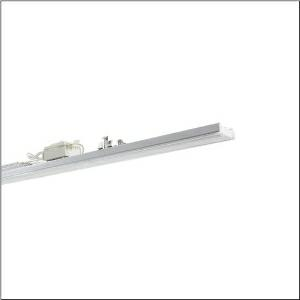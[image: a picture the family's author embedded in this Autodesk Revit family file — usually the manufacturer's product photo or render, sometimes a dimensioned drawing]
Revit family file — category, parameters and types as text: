
# Revit family: licross_r__21_recessed_ho_52tl1edn4e5s_7fa6
name_source: partatom
category: Lighting Fixtures
units: mm (PartAtom-declared; Revit-internal decimal feet)

## family parameters
Cut with Voids When Loaded = No
Host = Face
Light Source = No
Part Type = Normal
Room Calculation Point = No
Round Connector Dimension = Use Diameter
Shared = No

## types (1)
- --- (1 x LED, 14620 lm, 84.6 W, 4000K)
    Apparent Load = 85 VA
    CIE Flux Codes = 85 95 99 100 100
    Color Rendering = 80
    Color Temperature = 4000K
    Default Elevation = 1800 mm
    Description = Licross® 21 Recessed HO, luminaire insert, of sheet steel, galvanised, coil coated, white, length: 1.500mm, width: 66mm, height: 67mm, LED rated luminous flux: 14.620lm, light colour: 840, control gear: DALI 2, with plug, 5-pole, with phase selection, mains connection: 220..240V, AC, 50/60Hz, rated input power: 85W, internal wiring halogen-free, primary light control with lens, of plastic, primary optical cover: cover, of PMMA, light emission: direct distribution, primary light characteristic: symmetric, protection rating (complete): IP40, insulation class (complete): insulation class I (protective earthing), certification: CE, ENEC, VDE, UKCA, protection symbol: D if used in an environment without relevant dust loads with corresponding accessories, impact resistance: IK06, permissible ambient temperature for indoor applications: -25..+30°C, corresponds to IFS (International Featured Standards) requirements for safety and quality in the food industry, reducing of maximum allowable ambient temperature of 5°C with ceiling mounting, LABS conformity tested according to VDMA 24364:2018-05, packaging unit: 1 piece
    Height = 58 mm
    Lamp = 1 x LED
    Lamp Light Flux = 14620 lm
    Lamp Power = 84.6 W
    Lamp count = 1
    Length = 1500 mm
    Luminous efficacy = 173 lm/W
    Manufacturer = Siteco
    ModVariant = No
    Model = 52TL1EDN4E5S
    Mounting Place = Ceiling
    Mounting Type = Pendant
    Number of Poles = 1
    OnlyDefault = Yes
    Power Factor = 1
    Product Name = Licross® 21 Recessed HO
    Product group = luminaire insert | ceiling pendant
    ProductGroupID = 902
    Protection Class = Protection class I
    Protection Degree = IP 40
    RLX_Detail_Level = 1
    RLX_Emergency_Light_Flux = 0 lm
    RLX_Emergency_Type = 0
    RLX_Emergency_Type_DB = No
    RlxData = <blob elided: 24789 chars, md5=5c275dd9>
    Socket = socket
    Standby Power = 0 W
    System Light Flux = 14620 lm
    System Power = 85 W
    Type Comments = factory setting: luminous flux: 100 % | dim-lin: 254 | 484 mA
    Type Image = l_1296930.jpg
    URL = http://relux.com
    VarID = @adj_146699
    Voltage = 0 V
    Weight = 0.00 kg
    Width = 66 mm

## geometry (parser evidence)
native form markers: Blend x4, Sweep x11
no freeform markers — native parametric forms only
